# Revit family: Drinking_Fountain-Haws_Corporation-Wall_Mounted_1107L new new
name_source: partatom
category: Plumbing Fixtures
revit_build: Autodesk Revit Architecture 2015 (Build: 20160512_1515(x64)
units: mm (PartAtom-declared; Revit-internal decimal feet)

## types (3) — shared parameters
Assembly Code = D2010810
Back Plate = Metal - Haws Corporation - Polished Chrome - 5703M
Basin Height = 0' - 4 1/4"
Basin Width = 1' - 0"
Bowl = Metal - Haws Corporation - Polished Chrome - 5703M
CW Connection = Yes
Cost Note = For Cost information please visit the Resource tab in the Product Page URL
Default Elevation = 0' - 3 1/8"
Flow = 0 GPM
HW Connection = No
Keynote = 15410.A1
Manufacturer = Haws Corporation
Product Documentation Link = https://www.hawsco.com
Product Page URL = http://www.hawsco.com
Sanitary Radius = 0' - 0 5/8"
Series = The Haws 1107 low profile barrier free drinking fountain with antimicrobial protection
Supply Radius = 0' - 0 3/16"
Trim = Metal - Haws Corporation - Polished Chrome - 5703M
URL = http://www.hawsco.com
Version = 2014-v2.0a
WFU = 1
Waste Connection = Yes
zero-valued in all types: Cost, HWFU

## per-type parameters (varying)
| type | CWFU | Description | Trim Plate | Type Comments | Vent Connection |
| 1107LBP | 2 | With internal trap allows the 1107L to be placed securely in multiple locations | No | Designed including a back panel | Yes |
| 1107L | 1 | With internal trap allows the 1107L to be placed securely in multiple locations | No | Designed without a back panel | No |
| H1107.8 | 3 | Outfitted with such protective features as vandal-resistant bubbler head, waste strainer, and bottom plate | Yes | Electric drinking fountain with antimicrobial protection* provides 8 gph chilled water performance | Yes |

note: column(s) folded — value = type name in every type: Model

## geometry (parser evidence)
native form markers: Blend x8, Sweep x5
no freeform markers — native parametric forms only
